# Revit family: Specialty_Equipment-Detroit_Radiant-Unit_Heater-UH_Series-rev
name_source: partatom
category: Specialty Equipment
units: mm (PartAtom-declared; Revit-internal decimal feet)

## family parameters
Always vertical = Yes
Cut with Voids When Loaded = No
Enable Cutting in Views = No
Maintain Annotation Orientation = No
OmniClass Number = 23.75.00.00
OmniClass Title = Climate Control (HVAC)
Part Type = Normal
Room Calculation Point = No
Round Connector Dimension = Use Diameter
Shared = No
Work Plane-Based = No

## types (4) — shared parameters
Assembly Code = D3020
CD_Exhaust Offset H = 0' - 8 1/2"
CD_Fan Depth = 0' - 6 1/2"
CD_Finish = Metal-Steel-Detroit_Radiant-Coated_Aluminized_Steel
CD_Finish Component = Metal-Steel-Detroit_Radiant-Stainless
CD_Heater Depth = 1' - 5"
CD_Install Documentation = https://www.reverberray.com
CD_Microsite = https://www.caddetails.com
CD_Product Documentation Link = https://www.reverberray.com
CD_Product Name = Separated Combustion, Gas-Fired Unit Heater
CD_Product Page URL = https://www.reverberray.com
CD_Unit Size = Description of Product Sizing, set with equation if possible
CH_Heater Width = 2' - 4"
Description = Separated Combustion, Gas-Fired Unit Heater
Manufacturer = Detroit Radiant Products Company
URL = https://www.reverberray.com

## per-type parameters (varying)
| type | CD_Exhaust Offset W | CD_Fan Offset W | CD_Fan Radius | CD_Gas Connector | CD_Gas Offset H | CD_Gas Offset W | CD_Heater Height | CD_Louver Spacing | CD_Number of Louvers | CD_Vent Offset H | CD_Vent Offset W | CD_Void Offset Left | CD_Void Offset Right | Default Elevation | UH30 | UH45 | UH60 | UH75 |
| UH-30 | 0' - 8 1/2" | 0' - 7" | 0' - 5" | 30,000 BTU | 0' - 9 1/2" | 0' - 4" | 1' - 0" | 0' - 2 1/2" | 4 | 0' - 4" | 0' - 5 1/2" | 1' - 0" | 0' - 1" | 8' - 0" | Yes | No | No | No |
| UH-45 | 0' - 8 1/2" | 0' - 7" | 0' - 5" | 45,000 BTU | 0' - 9 1/2" | 0' - 4" | 1' - 0" | 0' - 2 1/2" | 4 | 0' - 4" | 0' - 5 1/2" | 1' - 0" | 0' - 1" | 8' - 0" | No | Yes | No | No |
| UH-60 | 1' - 7" | 1' - 7 1/2" | 0' - 7" | 60,000 BTU | 0' - 4" | 2' - 0" | 1' - 5" | 0' - 3" | 5 | 1' - 1" | 1' - 11" | 0' - 1" | 1' - 0" | 10' - 0" | No | No | Yes | No |
| UH-75 | 1' - 7" | 1' - 7 1/2" | 0' - 7" | 75,000 BTU | 0' - 4" | 2' - 0" | 1' - 5" | 0' - 3" | 5 | 1' - 1" | 1' - 11" | 0' - 1" | 1' - 0" | 10' - 0" | No | No | No | Yes |

note: column(s) folded — value = type name in every type: Model

## geometry (parser evidence)
native form markers: Sweep x4
no freeform markers — native parametric forms only
